# Revit family: LO
name_source: partatom
category: Communication Devices
revit_build: Autodesk Revit 2014 (Build: 20130308_1515(x64)
units: mm (PartAtom-declared; Revit-internal decimal feet)

## types (1)
- LO
    Assembly Code = D5090
    Certifications = UL and cUL listed
    Default Elevation = 48 "
    Description = The LOIR sensor uses passive infrared (PIR) technology to turn lighting on and off based on occupancy. Designed specifically for areas with long-range major-motion activity, this sensor features Hubbell Control Solutions' patented IntelliDAPT technology, which makes all the sensor adjustments automatically. Throughout the product's lifespan, smart software analyzes the controlled area and makes digital adjustments to sensitivity and timer settings. Occupancy sensors with IntelliDAPT provide a maintenance-free Install and Forget operation.
    Feartures = IntelliDAPT self-adaptive technology; no manual adjustment required
All-digital passive infrared (PIR) sensor
Non-volatile memory for sensor settings
50’ @ 30’ height coverage area
Optional relay and photocell control
Optional Quick to Install (QTI) connector
UL and cUL listed
5-year warranty
    Housing Material = Paint - Hubbell - Matte White
    Manufacturer = Hubbell Control Solutions
    Model = LightOWL® Passive Infrared Wall Mount Sensor
    Power Requirements = 24VDC, 33 mA (uses UVPP and MP-Series
power pack—not included)
    Product Documentation Link = https://hubbellcdn.com
    Product Page URL = https://www.hubbell.com
    Sensing Element = Metal-Hubbell-Nickel
    Type Comments = LightOWL® Passive Infrared Wall Mount Sensor
    URL = https://www.hubbell.com
    Warranty = 5-Years Warranty

## geometry (parser evidence)
native form markers: Sweep x3
no freeform markers — native parametric forms only
